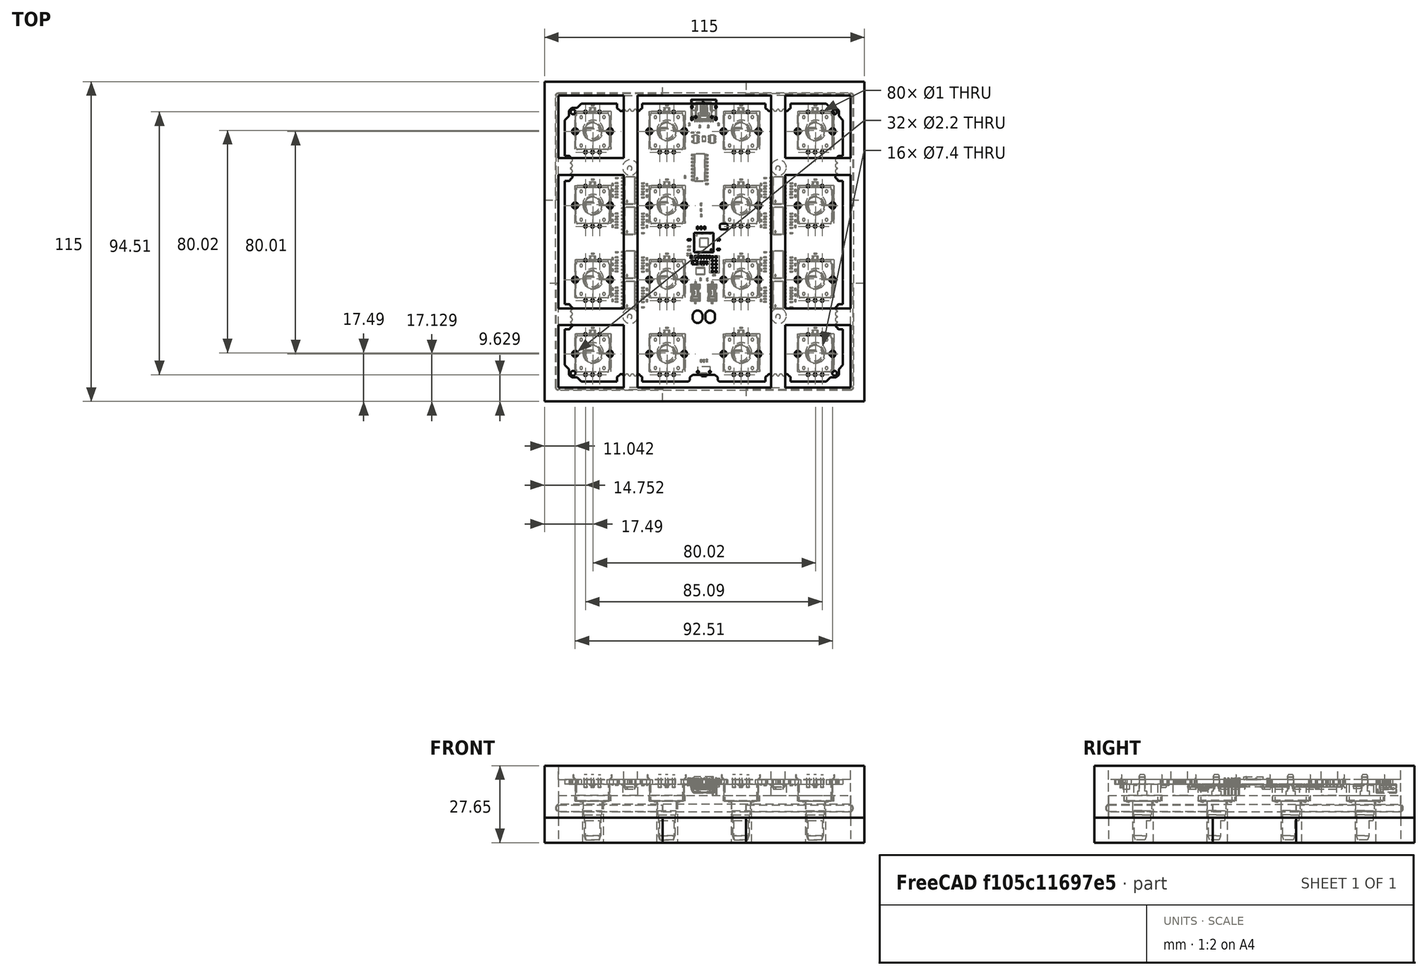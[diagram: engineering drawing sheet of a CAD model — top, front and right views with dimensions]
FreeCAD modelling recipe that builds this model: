
FCSTD DOCUMENT  (FreeCAD 0.21R33668 +26 (Git))
Label: EN16_solder_jig_assy
License: All rights reserved
LicenseURL: https://en.wikipedia.org/wiki/All_rights_reserved
objects: App::FeaturePython×4, Sketcher::SketchObject×3, PartDesign::Plane×2, Part::FeaturePython×2, PartDesign::Body×1
note: 8 computed .brp shape members not serialized (recipe doc carries the construction recipe); baked Part::Feature solids carry a one-line shape summary decoded from their .brp

FEATURE [PartDesign::Plane] DatumPlane
  AttachmentOffset = pos=(0,0,6) rot=(0,0,1;0rad)
  Length = 60.198
  MapMode = 5
  Placement = pos=(0,0,6) rot=(0,0,1;0rad)
  ResizeMode = 0
  Support = -> [XY_Plane]
  Width = 62.198
FEATURE [Sketcher::SketchObject] Sketch
  FullyConstrained = true
  MapMode = 5
  Placement = pos=(0,0,6) rot=(0,0,1;0rad)
  Support = -> [DatumPlane]
FEATURE [Part::FeaturePython] b_PCBA_EN16_3D1_001_  label="PCBA-EN16-3D1_001"  # a2plus imported part (geometry in sourceFile) (typed FeaturePython)
  Placement = pos=(-0.203049,-0.366159,7.65) rot=(0,1,0;3.14159rad)
  a2p_Version = 0.4.61
  fixedPosition = false
  objectType = a2pPart
  sourceFile = .\..\Mechanical\Design\Assembly\PCBA steps for assy\PCBA-EN16-3D.step
  subassemblyImport = false
  timeLastImport = 1.70308e+09
  updateColors = true
FEATURE [Part::FeaturePython] b_EN16_solder_jig_m_xc3_xa1solata_001_  label="EN16_solder_jig másolata_001"  # a2plus imported part (geometry in sourceFile) (typed FeaturePython)
  a2p_Version = 0.4.61
  fixedPosition = true
  objectType = a2pPart
  sourceFile = .\EN16_solder_jig másolata.FCStd
  subassemblyImport = false
  timeLastImport = 1.71466e+09
  updateColors = true
FEATURE [App::FeaturePython] planeCoincident_001  label="planeCoincident_001__EN16_solder_jig másolata_001"  # a2plus constraint (typed FeaturePython)
  Object1 = b_PCBA_EN16_3D1_001_
  Object2 = b_EN16_solder_jig_m_xc3_xa1solata_001_
  ParentTreeObject = -> b_PCBA_EN16_3D1_001_
  SubElement1 = Face1361
  SubElement2 = Face67
  Suppressed = false
  Type = plane
  directionConstraint = 0
  offset = 0
FEATURE [App::FeaturePython] planeCoincident_001_mirror  label="planeCoincident_001__PCBA-EN16-3D1_001"  # a2plus constraint (typed FeaturePython)
  Object1 = b_PCBA_EN16_3D1_001_
  Object2 = b_EN16_solder_jig_m_xc3_xa1solata_001_
  ParentTreeObject = -> b_EN16_solder_jig_m_xc3_xa1solata_001_
  SubElement1 = Face1361
  SubElement2 = Face67
  Suppressed = false
  Type = plane
  directionConstraint = 0
  offset = 0
FEATURE [App::FeaturePython] axisCoincident_001  label="axisCoincident_001__EN16_solder_jig másolata_001"  # a2plus constraint (typed FeaturePython)
  Object1 = b_PCBA_EN16_3D1_001_
  Object2 = b_EN16_solder_jig_m_xc3_xa1solata_001_
  ParentTreeObject = -> b_PCBA_EN16_3D1_001_
  SubElement1 = Edge9226
  SubElement2 = Edge267
  Suppressed = false
  Type = axial
  directionConstraint = 1
  lockRotation = false
FEATURE [App::FeaturePython] axisCoincident_001_mirror  label="axisCoincident_001__PCBA-EN16-3D1_001"  # a2plus constraint (typed FeaturePython)
  Object1 = b_PCBA_EN16_3D1_001_
  Object2 = b_EN16_solder_jig_m_xc3_xa1solata_001_
  ParentTreeObject = -> b_EN16_solder_jig_m_xc3_xa1solata_001_
  SubElement1 = Edge9226
  SubElement2 = Edge267
  Suppressed = false
  Type = axial
  directionConstraint = 1
  lockRotation = false
FEATURE [Sketcher::SketchObject] Sketch001
  FullyConstrained = true
  MapMode = 5
  Placement = pos=(0,0,0) rot=(1,0,0;1.5708rad)
  Support = -> [XZ_Plane]
FEATURE [PartDesign::Plane] DatumPlane001
  AttachmentOffset = pos=(0,0,27) rot=(0,0,1;0rad)
  Length = 60
  MapMode = 5
  Placement = pos=(0,-27,6e-15) rot=(1,0,0;1.5708rad)
  ResizeMode = 0
  Support = -> [XZ_Plane]
  Width = 60
FEATURE [Sketcher::SketchObject] Sketch002
  FullyConstrained = true
  MapMode = 5
  Placement = pos=(0,-27,6e-15) rot=(1,0,0;1.5708rad)
  Support = -> [DatumPlane001]
FEATURE [PartDesign::Body] Body
  Group = -> [DatumPlane,Sketch,Sketch001,DatumPlane001,Sketch002]
  Origin = -> Origin
